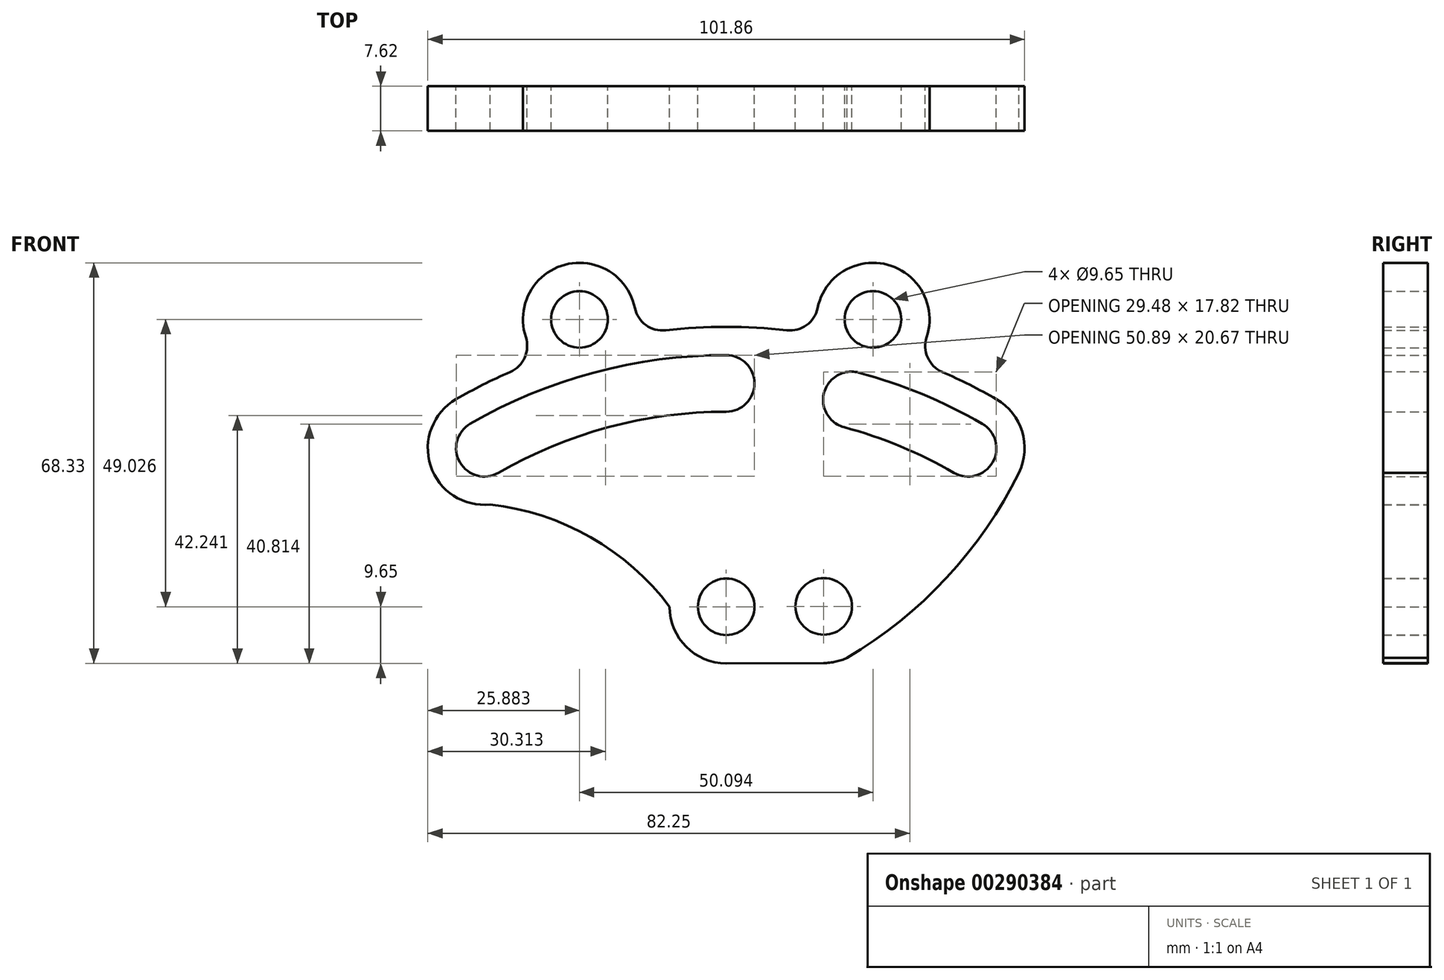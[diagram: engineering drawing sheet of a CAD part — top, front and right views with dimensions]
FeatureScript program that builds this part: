
annotation { "Feature Type Name" : "Feature", "Feature Type Description" : "" }
export const myFeature = defineFeature(function(context is Context, id is Id, definition is map)
    precondition{}
    {
        {
            var Q0;
            Q0=qCreatedBy(makeId("Front.planeOp"),FACE);
            var sketch = newSketch(context, id + "F0", { "sketchPlane" : qUnion([Q0])});
            skArc(sketch, "E0", {"start": v(68.74, 68.12) * mm, "mid": v(-2.55, 96.74) * mm, "end": v(-72.23, 64.4) * mm, "construction": true});
            skArc(sketch, "E1", {"start": v(46.1, 79.85) * mm, "mid": v(41.55, 82.31) * mm, "end": v(36.86, 84.51) * mm});
            skArc(sketch, "E2", {"start": v(64.4, 51.65) * mm, "mid": v(-2.45, 82.51) * mm, "end": v(-67.35, 47.74) * mm, "construction": true});
            skLineSegment(sketch, "E3", {"start": v(0, 0) * mm, "end": v(0, 118.2) * mm, "construction": true});
            skLineSegment(sketch, "E4", {"start": v(0, 0) * mm, "end": v(-30.78, 114.87) * mm, "construction": true});
            skLineSegment(sketch, "E5", {"start": v(0, 0) * mm, "end": v(-60.6, 104.97) * mm, "construction": true});
            skLineSegment(sketch, "E6", {"start": v(0, 0) * mm, "end": v(30.34, 113.22) * mm, "construction": true});
            skLineSegment(sketch, "E7", {"start": v(0, 0) * mm, "end": v(58.42, 101.18) * mm, "construction": true});
            skArc(sketch, "E8", {"start": v(-15.6, 95.44) * mm, "mid": v(-27.55, 102.8) * mm, "end": v(-34.21, 90.45) * mm});
            skArc(sketch, "E9", {"start": v(34.21, 90.45) * mm, "mid": v(27.55, 102.8) * mm, "end": v(15.6, 95.44) * mm});
            skCircle(sketch, "E10", {"center": v(25.05, 93.48) * mm, "radius": 4.83 * mm});
            skCircle(sketch, "E11", {"center": v(-25.05, 93.48) * mm, "radius": 4.83 * mm});
            skArc(sketch, "E12", {"start": v(-43.69, 75.67) * mm, "mid": v(-45.45, 69.08) * mm, "end": v(-38.86, 67.31) * mm});
            skArc(sketch, "E13", {"start": v(0, 77.72) * mm, "mid": v(4.83, 82.55) * mm, "end": v(0, 87.38) * mm});
            skArc(sketch, "E14", {"start": v(22.61, 84.4) * mm, "mid": v(16.7, 80.99) * mm, "end": v(20.12, 75.08) * mm});
            skArc(sketch, "E15", {"start": v(38.86, 67.31) * mm, "mid": v(45.45, 69.08) * mm, "end": v(43.69, 75.67) * mm});
            skArc(sketch, "E16", {"start": v(-38.86, 67.31) * mm, "mid": v(-20.12, 75.08) * mm, "end": v(0, 77.72) * mm});
            skArc(sketch, "E17", {"start": v(-43.69, 75.67) * mm, "mid": v(-22.61, 84.4) * mm, "end": v(0, 87.38) * mm});
            skArc(sketch, "E18.trimOffspring", {"start": v(22.61, 84.4) * mm, "mid": v(33.44, 80.72) * mm, "end": v(43.69, 75.67) * mm});
            skArc(sketch, "E19.trimOffspring", {"start": v(20.12, 75.08) * mm, "mid": v(29.74, 71.8) * mm, "end": v(38.86, 67.31) * mm});
            skArc(sketch, "E20.filletArc", {"start": v(-15.6, 95.44) * mm, "mid": v(-13.7, 92.5) * mm, "end": v(-10.33, 91.62) * mm});
            skArc(sketch, "E21.filletArc", {"start": v(34.21, 90.45) * mm, "mid": v(34.39, 86.97) * mm, "end": v(36.86, 84.51) * mm});
            skArc(sketch, "E22", {"start": v(10.33, 91.62) * mm, "mid": v(0, 92.2) * mm, "end": v(-10.33, 91.62) * mm});
            skArc(sketch, "E23.filletArc", {"start": v(10.33, 91.62) * mm, "mid": v(13.7, 92.5) * mm, "end": v(15.6, 95.44) * mm});
            skArc(sketch, "E24.trimOffspring", {"start": v(-36.86, 84.51) * mm, "mid": v(-41.55, 82.31) * mm, "end": v(-46.1, 79.85) * mm});
            skArc(sketch, "E25.filletArc", {"start": v(-36.86, 84.51) * mm, "mid": v(-34.39, 86.97) * mm, "end": v(-34.21, 90.45) * mm});
            skArc(sketch, "E26", {"start": v(-46.1, 79.85) * mm, "mid": v(-50.46, 68.51) * mm, "end": v(-40.28, 61.89) * mm});
            skArc(sketch, "E27", {"start": v(49.34, 66.18) * mm, "mid": v(50.67, 73.71) * mm, "end": v(46.1, 79.85) * mm});
            skLineSegment(sketch, "E28", {"start": v(0, 0) * mm, "end": v(0, 44.45) * mm});
            skCircle(sketch, "E29", {"center": v(0, 44.45) * mm, "radius": 4.83 * mm});
            skCircle(sketch, "E30", {"center": v(16.63, 44.5) * mm, "radius": 4.83 * mm});
            skArc(sketch, "E31", {"start": v(16.63, 34.85) * mm, "mid": v(19.83, 35.4) * mm, "end": v(22.67, 36.98) * mm});
            skArc(sketch, "E32", {"start": v(-9.65, 44.45) * mm, "mid": v(-6.82, 37.63) * mm, "end": v(0, 34.8) * mm});
            skArc(sketch, "E33", {"start": v(20.62, 35.72) * mm, "mid": v(37.58, 49.4) * mm, "end": v(49.98, 67.31) * mm});
            skLineSegment(sketch, "E34", {"start": v(16.63, 34.85) * mm, "end": v(0, 34.8) * mm});
            skArc(sketch, "E35", {"start": v(-9.65, 44.45) * mm, "mid": v(-23.16, 56.34) * mm, "end": v(-40.28, 61.89) * mm});
            skSolve(sketch);
        }
        {
            var Q0;
            {var subQ1=sQuery(id+"F0.wireOp",EDGE,"E1");Q0=makeQuery(id+"F0.imprint","IMPRINT",FACE,{"disambiguationData":[TD([[makeQuery(id+"F0.imprint","IMPRINT",EDGE,{"derivedFrom":subQ1}),1.0]])]});}
            extrude(context, id + "F1", {"entities" : qUnion([Q0]), "depth" : 7.62 * mm});
        }
    });
